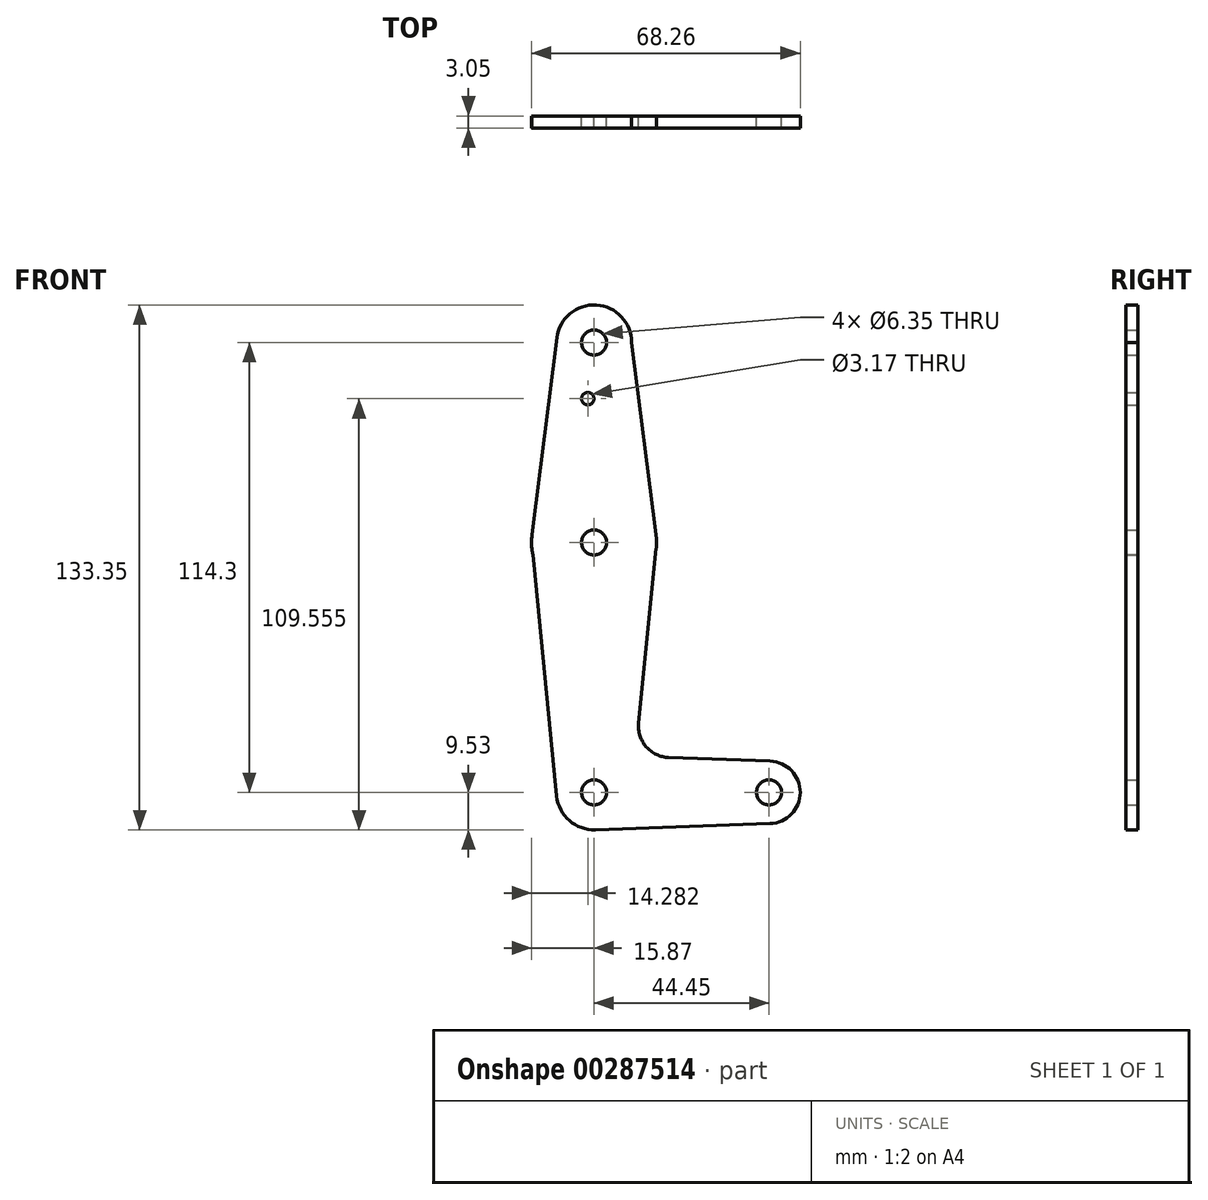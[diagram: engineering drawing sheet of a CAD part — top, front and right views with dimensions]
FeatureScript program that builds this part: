
annotation { "Feature Type Name" : "Feature", "Feature Type Description" : "" }
export const myFeature = defineFeature(function(context is Context, id is Id, definition is map)
    precondition{}
    {
        {
            var Q0;
            Q0=qCreatedBy(makeId("Front.planeOp"),FACE);
            var sketch = newSketch(context, id + "F0", { "sketchPlane" : qUnion([Q0])});
            skLineSegment(sketch, "E0", {"start": v(0, 50.8) * mm, "end": v(0, -63.5) * mm, "construction": true});
            skLineSegment(sketch, "E1", {"start": v(0, -63.5) * mm, "end": v(44.45, -63.5) * mm, "construction": true});
            skCircle(sketch, "E2", {"center": v(0, 50.8) * mm, "radius": 9.53 * mm});
            skCircle(sketch, "E3", {"center": v(0, 0) * mm, "radius": 15.88 * mm});
            skCircle(sketch, "E4", {"center": v(0, -63.5) * mm, "radius": 9.53 * mm});
            skCircle(sketch, "E5", {"center": v(44.45, -63.5) * mm, "radius": 7.94 * mm});
            skLineSegment(sketch, "E6", {"start": v(-9.45, 52) * mm, "end": v(-15.75, 2) * mm});
            skLineSegment(sketch, "E7", {"start": v(9.52, 50.8) * mm, "end": v(15.75, 2) * mm});
            skLineSegment(sketch, "E8", {"start": v(-15.88, 0) * mm, "end": v(-9.48, -64.44) * mm});
            skCircle(sketch, "E9", {"center": v(0, 50.8) * mm, "radius": 3.18 * mm});
            skCircle(sketch, "E10", {"center": v(0, 0) * mm, "radius": 3.18 * mm});
            skCircle(sketch, "E11", {"center": v(0, -63.5) * mm, "radius": 3.18 * mm});
            skCircle(sketch, "E12", {"center": v(44.45, -63.5) * mm, "radius": 3.18 * mm});
            skCircle(sketch, "E13", {"center": v(-1.59, 36.53) * mm, "radius": 1.59 * mm});
            skLineSegment(sketch, "E14", {"start": v(0.34, -73.02) * mm, "end": v(44.73, -71.43) * mm});
            skLineSegment(sketch, "E15", {"start": v(15.8, -1.59) * mm, "end": v(11.34, -45.9) * mm});
            skLineSegment(sketch, "E16", {"start": v(18.97, -54.65) * mm, "end": v(44.73, -55.57) * mm});
            skArc(sketch, "E17.filletArc", {"start": v(11.34, -45.9) * mm, "mid": v(13.26, -51.93) * mm, "end": v(18.97, -54.65) * mm});
            skSolve(sketch);
        }
        {
            var Q0;
            Q0 = qSketchRegion(id + "F0", true);
            extrude(context, id + "F1", {"entities" : qUnion([Q0]), "depth" : 3.05 * mm});
        }
    });
